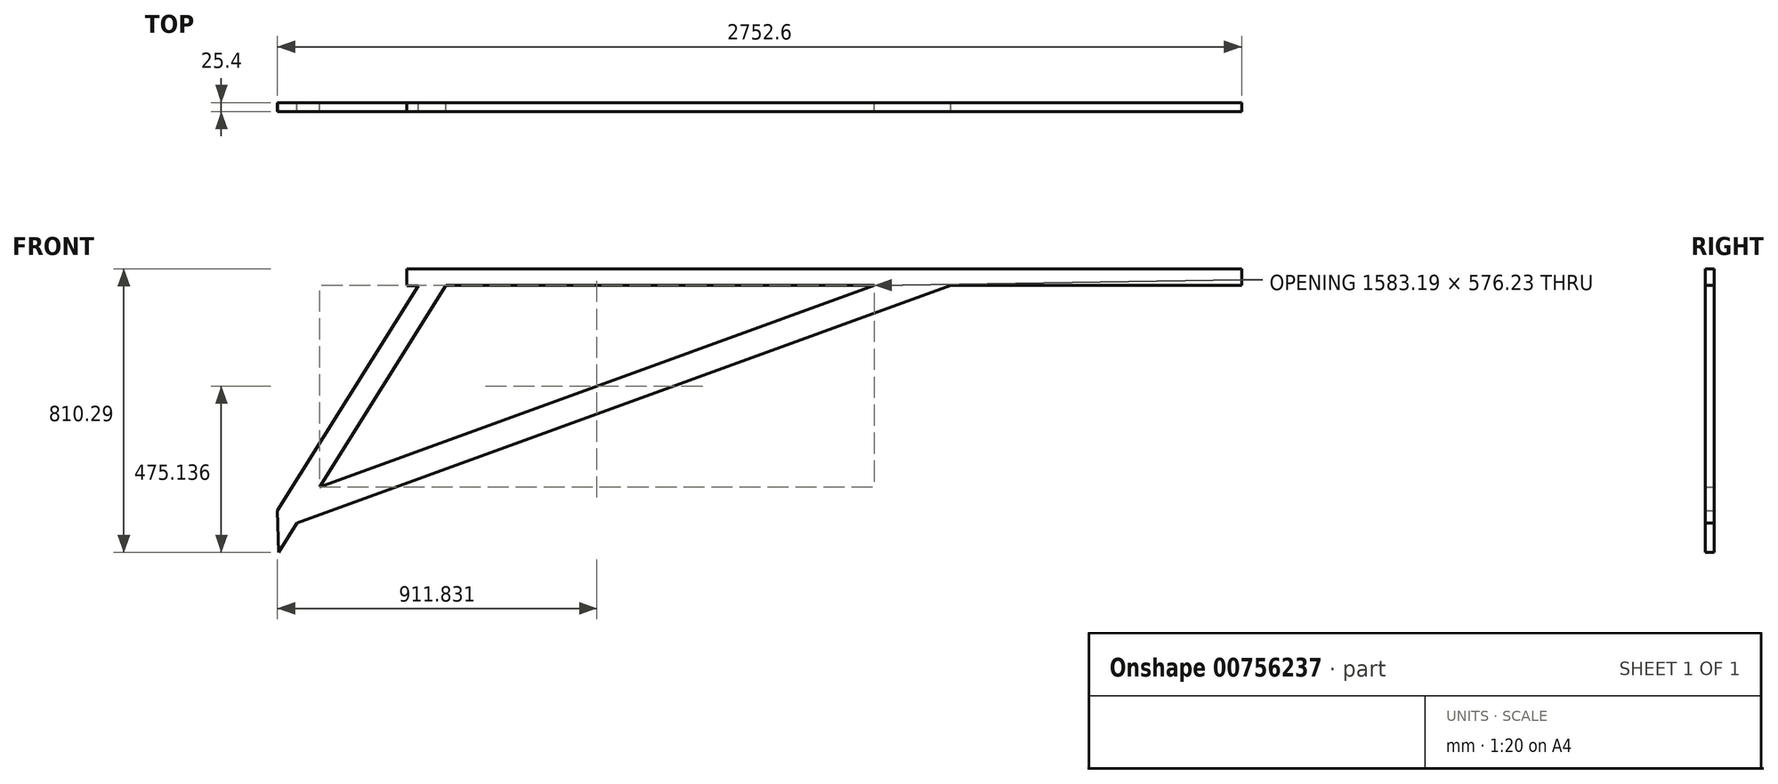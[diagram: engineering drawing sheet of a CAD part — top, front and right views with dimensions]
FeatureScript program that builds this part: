
annotation { "Feature Type Name" : "Feature", "Feature Type Description" : "" }
export const myFeature = defineFeature(function(context is Context, id is Id, definition is map)
    precondition{}
    {
        {
            var Q0;
            Q0=qCreatedBy(makeId("Front.planeOp"),FACE);
            var sketch = newSketch(context, id + "F0", { "sketchPlane" : qUnion([Q0])});
            skLineSegment(sketch, "E0.bottom", {"start": v(-598.98, -94.25) * mm, "end": v(1306.02, -94.25) * mm});
            skLineSegment(sketch, "E0.top", {"start": v(-598.98, -141.29) * mm, "end": v(1306.02, -141.29) * mm});
            skLineSegment(sketch, "E0.left", {"start": v(-598.98, -94.25) * mm, "end": v(-598.98, -141.29) * mm});
            skLineSegment(sketch, "E0.right", {"start": v(1306.02, -94.25) * mm, "end": v(1306.02, -141.29) * mm});
            skLineSegment(sketch, "E1", {"start": v(-598.98, -141.29) * mm, "end": v(-966.27, -141.29) * mm});
            skLineSegment(sketch, "E2", {"start": v(-966.27, -141.29) * mm, "end": v(475.2, -141.29) * mm});
            skLineSegment(sketch, "E3", {"start": v(475.2, -141.29) * mm, "end": v(-1390.63, -820.4) * mm});
            skLineSegment(sketch, "E4", {"start": v(-966.27, -141.29) * mm, "end": v(-1443.2, -904.54) * mm});
            skLineSegment(sketch, "E5", {"start": v(-1446.58, -784.92) * mm, "end": v(-1443.2, -904.54) * mm});
            skLineSegment(sketch, "E6", {"start": v(-1326.34, -717.52) * mm, "end": v(256.85, -141.29) * mm});
            skLineSegment(sketch, "E7.bottom", {"start": v(-598.98, -94.25) * mm, "end": v(-1076.97, -94.25) * mm});
            skLineSegment(sketch, "E7.top", {"start": v(-598.98, -142.25) * mm, "end": v(-1076.97, -142.25) * mm});
            skLineSegment(sketch, "E7.left", {"start": v(-598.98, -94.25) * mm, "end": v(-598.98, -142.25) * mm});
            skLineSegment(sketch, "E7.right", {"start": v(-1076.97, -94.25) * mm, "end": v(-1076.97, -142.25) * mm});
            skLineSegment(sketch, "E8", {"start": v(-1446.58, -784.92) * mm, "end": v(-1045, -142.25) * mm});
            skSolve(sketch);
        }
        {
            var Q0;
            {var subQ6=sQuery(id+"F0.wireOp",EDGE,"E7.bottom");Q0=makeQuery(id+"F0.imprint","IMPRINT",FACE,{"disambiguationData":[TD([[makeQuery(id+"F0.imprint","IMPRINT",EDGE,{"derivedFrom":subQ6}),1.0]])]});}
            var Q1;
            {var subQ5=sQuery(id+"F0.wireOp",EDGE,"E0.bottom");Q1=makeQuery(id+"F0.imprint","IMPRINT",FACE,{"disambiguationData":[TD([[makeQuery(id+"F0.imprint","IMPRINT",EDGE,{"derivedFrom":subQ5}),-1.0]])]});}
            var Q2;
            {var subQ0=sQuery(id+"F0.wireOp",EDGE,"E3");Q2=makeQuery(id+"F0.imprint","IMPRINT",FACE,{"disambiguationData":[TD([[makeQuery(id+"F0.imprint","IMPRINT",EDGE,{"derivedFrom":subQ0}),-1.0]])]});}
            var Q3;
            {var subQ0=sQuery(id+"F0.wireOp",EDGE,"E5");Q3=makeQuery(id+"F0.imprint","IMPRINT",FACE,{"disambiguationData":[TD([[makeQuery(id+"F0.imprint","IMPRINT",EDGE,{"derivedFrom":subQ0}),1.0]])]});}
            extrude(context, id + "F1", {"entities" : qUnion([Q0, Q1, Q2, Q3]), "endBound" : BoundingType.SYMMETRIC, "depth" : 25.4 * mm, "offsetDistance" : 25.4 * mm});
        }
    });
